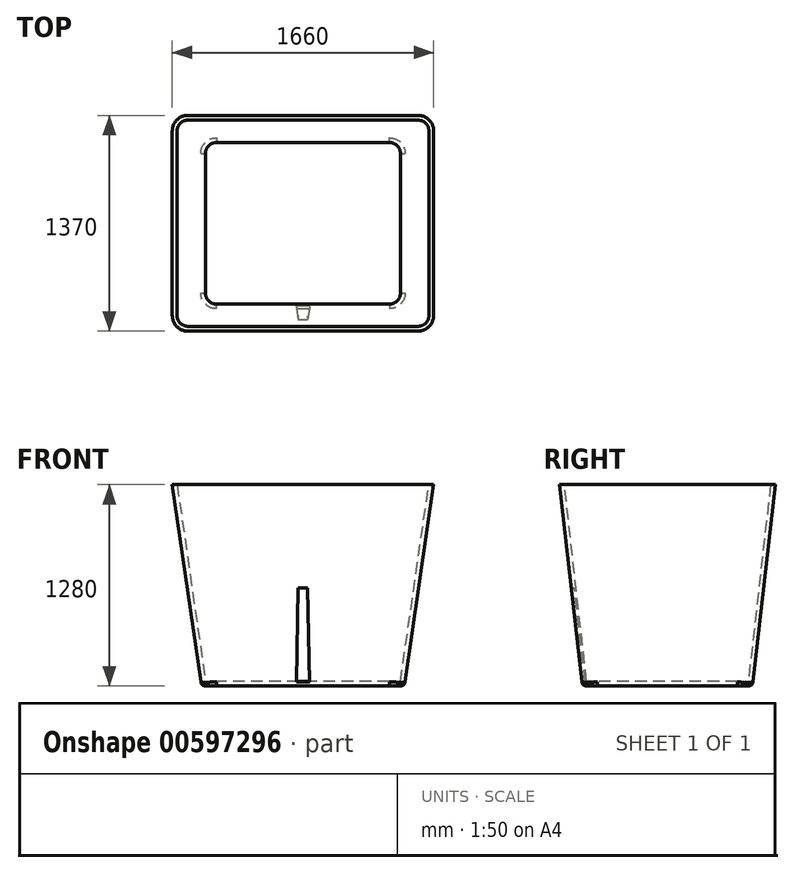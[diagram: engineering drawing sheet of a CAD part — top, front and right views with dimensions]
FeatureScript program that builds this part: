
annotation { "Feature Type Name" : "Feature", "Feature Type Description" : "" }
export const myFeature = defineFeature(function(context is Context, id is Id, definition is map)
    precondition{}
    {
        {
            var Q0;
            Q0=qCreatedBy(makeId("Top.planeOp"),FACE);
            var sketch = newSketch(context, id + "F0", { "sketchPlane" : qUnion([Q0])});
            skLineSegment(sketch, "E0.bottom", {"start": v(645, 540) * mm, "end": v(-645, 540) * mm});
            skLineSegment(sketch, "E0.top", {"start": v(645, -540) * mm, "end": v(-645, -540) * mm});
            skLineSegment(sketch, "E0.left", {"start": v(645, 540) * mm, "end": v(645, -540) * mm});
            skLineSegment(sketch, "E0.right", {"start": v(-645, 540) * mm, "end": v(-645, -540) * mm});
            skPoint(sketch, "E0.middle", {"position": v(0, 0) * mm});
            skSolve(sketch);
        }
        {
            var Q0;
            Q0=makeQuery(id+"F0.imprint","IMPRINT",FACE,{"disambiguationData":[TD([[makeQuery(id+"F0.imprint","IMPRINT",EDGE,{"derivedFrom":sQuery(id+"F0.wireOp",EDGE,"E0.bottom")}),1.0]])]});
            cPlane(context, id + "F1", {"entities" : qUnion([Q0]), "cplaneType" : CPlaneType.OFFSET, "offset" : 1280 * mm, "width" : 150 * mm, "height" : 150 * mm});
        }
        {
            var Q0;
            Q0=qCreatedBy(id+"F1.planeOp",FACE);
            var sketch = newSketch(context, id + "F2", { "sketchPlane" : qUnion([Q0])});
            skLineSegment(sketch, "E1.bottom", {"start": v(830, 685) * mm, "end": v(-830, 685) * mm});
            skLineSegment(sketch, "E1.top", {"start": v(830, -685) * mm, "end": v(-830, -685) * mm});
            skLineSegment(sketch, "E1.left", {"start": v(830, 685) * mm, "end": v(830, -685) * mm});
            skLineSegment(sketch, "E1.right", {"start": v(-830, 685) * mm, "end": v(-830, -685) * mm});
            skPoint(sketch, "E1.middle", {"position": v(0, 0) * mm});
            skSolve(sketch);
        }
        {
            var Q0;
            Q0=makeQuery(id+"F0.imprint","IMPRINT",FACE,{"disambiguationData":[TD([[makeQuery(id+"F0.imprint","IMPRINT",EDGE,{"derivedFrom":sQuery(id+"F0.wireOp",EDGE,"E0.bottom")}),1.0]])]});
            var Q1;
            Q1=makeQuery(id+"F2.imprint","IMPRINT",FACE,{"disambiguationData":[TD([[makeQuery(id+"F2.imprint","IMPRINT",EDGE,{"derivedFrom":sQuery(id+"F2.wireOp",EDGE,"E1.bottom")}),1.0]])]});
            loft(context, id + "F3", {"sheetProfilesArray" : [{ "sheetProfileEntities" : qUnion([Q0]) }, { "sheetProfileEntities" : qUnion([Q1]) }]});
        }
        {
            var Q0;
            Q0=makeQuery(id+"F3.opLoft","SWEPT_EDGE",EDGE,{"disambiguationData":[OSD([sQuery(id+"F0.wireOp",EDGE,"E0.top"),sQuery(id+"F0.wireOp",EDGE,"E0.left"),sQuery(id+"F2.wireOp",EDGE,"E1.top"),sQuery(id+"F2.wireOp",EDGE,"E1.left")])]});
            var Q1;
            Q1=makeQuery(id+"F3.opLoft","SWEPT_EDGE",EDGE,{"disambiguationData":[OSD([sQuery(id+"F0.wireOp",EDGE,"E0.bottom"),sQuery(id+"F0.wireOp",EDGE,"E0.left"),sQuery(id+"F2.wireOp",EDGE,"E1.bottom"),sQuery(id+"F2.wireOp",EDGE,"E1.left")])]});
            var Q2;
            Q2=makeQuery(id+"F3.opLoft","SWEPT_EDGE",EDGE,{"disambiguationData":[OSD([sQuery(id+"F0.wireOp",EDGE,"E0.top"),sQuery(id+"F0.wireOp",EDGE,"E0.right"),sQuery(id+"F2.wireOp",EDGE,"E1.top"),sQuery(id+"F2.wireOp",EDGE,"E1.right")])]});
            var Q3;
            Q3=makeQuery(id+"F3.opLoft","SWEPT_EDGE",EDGE,{"disambiguationData":[OSD([sQuery(id+"F0.wireOp",EDGE,"E0.bottom"),sQuery(id+"F0.wireOp",EDGE,"E0.right"),sQuery(id+"F2.wireOp",EDGE,"E1.bottom"),sQuery(id+"F2.wireOp",EDGE,"E1.right")])]});
            fillet(context, id + "F4", {"entities" : qUnion([Q0, Q1, Q2, Q3]), "radius" : 100 * mm, "tangentPropagation" : true, "allowEdgeOverflow" : false});
        }
        {
            var Q0;
            Q0=makeQuery(id+"F3.opLoft","CAP_FACE",FACE,{"disambiguationData":[OSD([makeQuery(id+"F2.imprint","IMPRINT",FACE,{"disambiguationData":[TD([[makeQuery(id+"F2.imprint","IMPRINT",EDGE,{"derivedFrom":sQuery(id+"F2.wireOp",EDGE,"E1.bottom")}),1.0]])]})])],"isStart":true});
            shell(context, id + "F5", {"entities" : qUnion([Q0]), "thickness" : 30 * mm});
        }
        {
            var Q0;
            {var subQ0=sQuery(id+"F0.wireOp",EDGE,"E0.top");var subQ1=sQuery(id+"F0.wireOp",EDGE,"E0.right");Q0=makeQuery(id+"F4.opFillet","BLEND_EDGE",EDGE,{"blendedFrom":[makeQuery(id+"F3.opLoft","SWEPT_EDGE",EDGE,{"disambiguationData":[OSD([subQ0,subQ1,sQuery(id+"F2.wireOp",EDGE,"E1.top"),sQuery(id+"F2.wireOp",EDGE,"E1.right")])]}),makeQuery(id+"F3.opLoft","CAP_FACE",FACE,{"disambiguationData":[OSD([makeQuery(id+"F0.imprint","IMPRINT",FACE,{"disambiguationData":[TD([[makeQuery(id+"F0.imprint","IMPRINT",EDGE,{"derivedFrom":sQuery(id+"F0.wireOp",EDGE,"E0.bottom")}),1.0]])]})])],"isStart":true})],"blendedInto":[makeQuery(id+"F3.opLoft","CAP_FACE",FACE,{"disambiguationData":[OSD([makeQuery(id+"F0.imprint","IMPRINT",FACE,{"disambiguationData":[TD([[makeQuery(id+"F0.imprint","IMPRINT",EDGE,{"derivedFrom":sQuery(id+"F0.wireOp",EDGE,"E0.bottom")}),1.0]])]})])],"isStart":true})]});}
            fillet(context, id + "F6", {"entities" : qUnion([Q0]), "radius" : 30 * mm, "tangentPropagation" : true, "allowEdgeOverflow" : false});
        }
        {
            var Q0;
            Q0=makeQuery(id+"F3.opLoft","SWEPT_FACE",FACE,{"disambiguationData":[OSD([sQuery(id+"F0.wireOp",EDGE,"E0.top"),sQuery(id+"F0.wireOp",EDGE,"E0.left"),sQuery(id+"F0.wireOp",EDGE,"E0.right"),sQuery(id+"F2.wireOp",EDGE,"E1.top"),sQuery(id+"F2.wireOp",EDGE,"E1.left"),sQuery(id+"F2.wireOp",EDGE,"E1.right")])]});
            var sketch = newSketch(context, id + "F7", { "sketchPlane" : qUnion([Q0])});
            skPoint(sketch, "E2.endSnap0", {"position": v(0, 87.58) * mm});
            skLineSegment(sketch, "E3", {"start": v(0, 687.58) * mm, "end": v(30, 687.58) * mm});
            skLineSegment(sketch, "E4", {"start": v(0, 87.58) * mm, "end": v(40, 87.58) * mm});
            skLineSegment(sketch, "E5", {"start": v(40, 87.58) * mm, "end": v(30, 687.58) * mm});
            skLineSegment(sketch, "E6.MirrorCS", {"start": v(0, 687.58) * mm, "end": v(-30, 687.58) * mm});
            skLineSegment(sketch, "E7.MirrorCS", {"start": v(-40, 87.58) * mm, "end": v(-30, 687.58) * mm});
            skSolve(sketch);
        }
        {
            var Q0;
            Q0 = qSketchRegion(id + "F7", true);
            var Q1;
            Q1=makeQuery(id+"F7.imprint","IMPRINT",FACE,{"disambiguationData":[TD([[makeQuery(id+"F7.imprint","IMPRINT",EDGE,{"derivedFrom":sQuery(id+"F7.wireOp",EDGE,"E3")}),-1.0]])]});
            extrude(context, id + "F8", {"entities" : qUnion([Q0, Q1]), "operationType" : NewBodyOperationType.REMOVE, "oppositeDirection" : true, "depth" : 20 * mm, "offsetDistance" : 25 * mm});
        }
        {
            var Q0;
            Q0=makeQuery(id+"F8.boolean.opBoolean","COPY",EDGE,{"derivedFrom":makeQuery(id+"F8.opExtrude","CAP_EDGE",EDGE,{"disambiguationData":[OSD([sQuery(id+"F7.wireOp",EDGE,"E7.MirrorCS")])],"isStart":true})});
            var Q1;
            Q1=makeQuery(id+"F8.boolean.opBoolean","COPY",EDGE,{"derivedFrom":makeQuery(id+"F8.opExtrude","CAP_EDGE",EDGE,{"disambiguationData":[OSD([sQuery(id+"F7.wireOp",EDGE,"E7.MirrorCS")])],"isStart":false})});
            var Q2;
            Q2=makeQuery(id+"F8.boolean.opBoolean","COPY",EDGE,{"derivedFrom":makeQuery(id+"F8.opExtrude","CAP_EDGE",EDGE,{"disambiguationData":[OSD([sQuery(id+"F7.wireOp",EDGE,"E5")])],"isStart":true})});
            var Q3;
            Q3=makeQuery(id+"F8.boolean.opBoolean","COPY",EDGE,{"derivedFrom":makeQuery(id+"F8.opExtrude","CAP_EDGE",EDGE,{"disambiguationData":[OSD([sQuery(id+"F7.wireOp",EDGE,"E3"),sQuery(id+"F7.wireOp",EDGE,"E6.MirrorCS")])],"isStart":true})});
            var Q4;
            Q4=makeQuery(id+"F8.boolean.opBoolean","COPY",EDGE,{"derivedFrom":makeQuery(id+"F8.opExtrude","CAP_EDGE",EDGE,{"disambiguationData":[OSD([sQuery(id+"F7.wireOp",EDGE,"E3"),sQuery(id+"F7.wireOp",EDGE,"E6.MirrorCS")])],"isStart":false})});
            var Q5;
            Q5=makeQuery(id+"F8.boolean.opBoolean","COPY",EDGE,{"derivedFrom":makeQuery(id+"F8.opExtrude","CAP_EDGE",EDGE,{"disambiguationData":[OSD([sQuery(id+"F7.wireOp",EDGE,"E5")])],"isStart":false})});
            fillet(context, id + "F9", {"entities" : qUnion([Q0, Q1, Q2, Q3, Q4, Q5]), "radius" : 5 * mm, "tangentPropagation" : true, "allowEdgeOverflow" : false});
        }
    });
